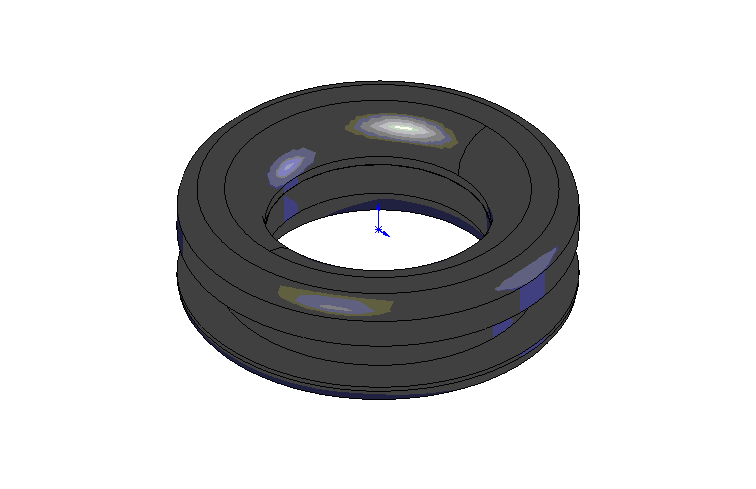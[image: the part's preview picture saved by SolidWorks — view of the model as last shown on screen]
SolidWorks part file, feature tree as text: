
SOLIDWORKS PART (.sldprt)
format: sldprt  version: not decoded by parser v0  size: 517,632 bytes
history: native  units: mm
features: sketch x4, fillet x4, plane x3, extrude x3, material x1, cut_extrude x1 (+10 scaffold rows collapsed)
feature tree (26):
  scaffold x10  (default folders/planes/origin — collapsed)
  material  "Matériau <non spécifié>"
  plane  "Plan de face"
  plane  "Plan de dessus"
  plane  "Plan de droite"
  sketch  "Esquisse1"  dims[c1.D4=300.0mm c1.D5=301.0mm c1.D2=302.0mm c1.D3=299.5mm c1.D1=8.0mm c2.D2=1.0mm c2.D3=0.5mm]
  extrude  "Extrusion1"  Depth=8mm
  sketch  "Esquisse2"
  cut_extrude  "Enlèv. mat.-Extru.1"  [1 undecoded]
  sketch  "Esquisse3"  dims[D1=6.5mm]
  extrude  "Extrusion2"  [1 undecoded]
  sketch  "Esquisse4"  dims[D1=4.5mm]
  extrude  "Enlèv. mat.-Extru.2"  [1 undecoded]
  fillet  "Congé1"  Radius=0.4mm
  fillet  "Congé3"  Radius=0.4mm
  fillet  "Congé5"  Radius=0.8mm
  fillet  "Congé6"  Radius=0.8mm
decode coverage: 8 of 12 modeling features carry decoded parameters
note: 3 parameter values undecoded
summary: no parameter record found for 3 features
note: suppression state not decoded; provenance and decode notes live in map.json
